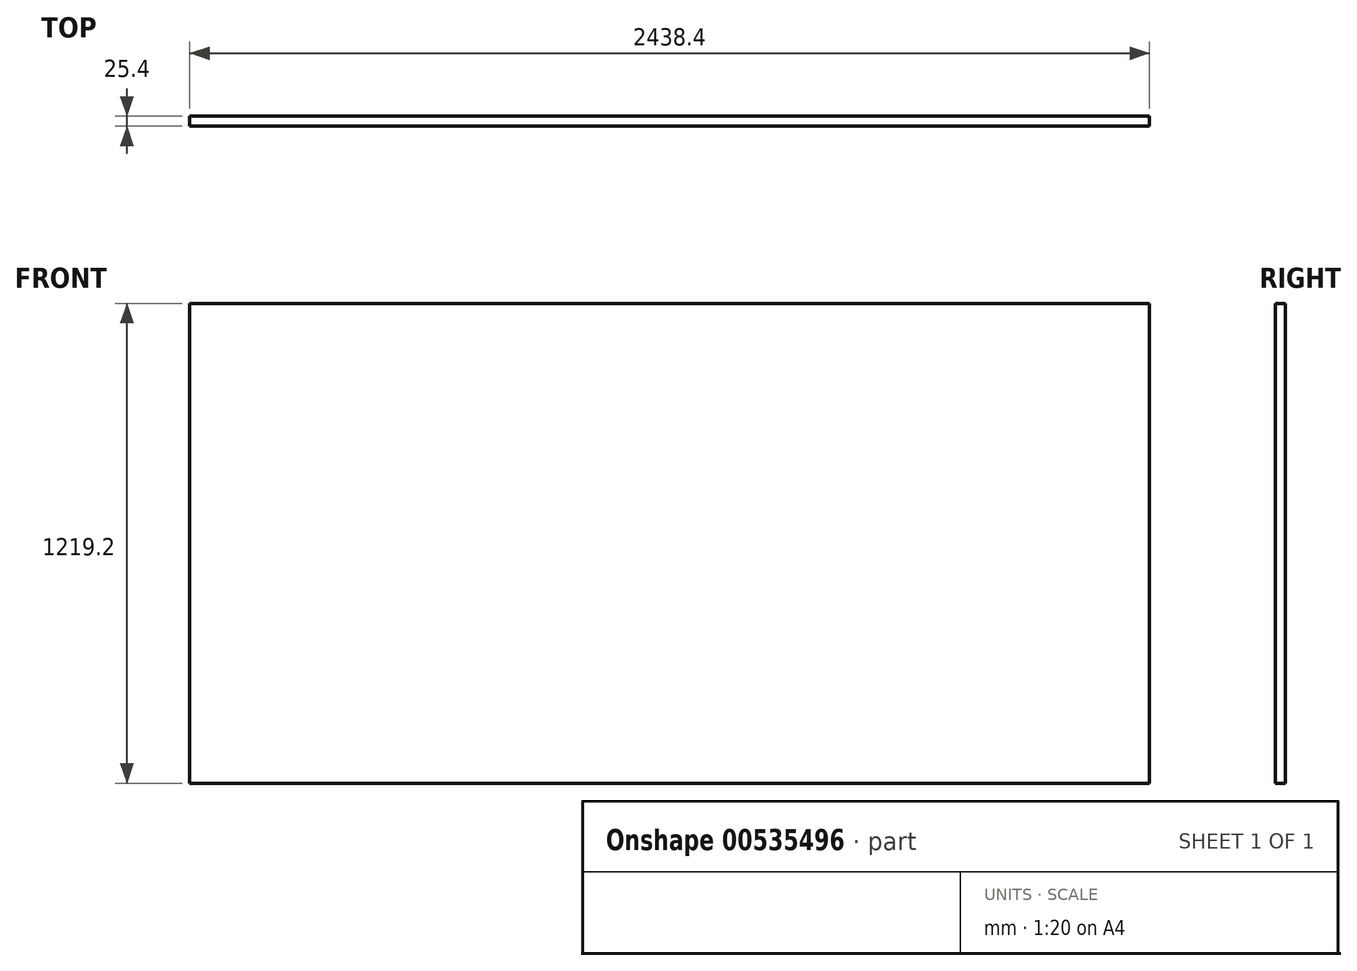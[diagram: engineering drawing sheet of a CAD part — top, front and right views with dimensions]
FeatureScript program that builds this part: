
annotation { "Feature Type Name" : "Feature", "Feature Type Description" : "" }
export const myFeature = defineFeature(function(context is Context, id is Id, definition is map)
    precondition{}
    {
        {
            var Q0;
            Q0=qCreatedBy(makeId("Front.planeOp"),FACE);
            var sketch = newSketch(context, id + "F0", { "sketchPlane" : qUnion([Q0])});
            skLineSegment(sketch, "E0.bottom", {"start": v(-1334.16, 605.52) * mm, "end": v(1104.24, 605.52) * mm});
            skLineSegment(sketch, "E0.top", {"start": v(-1334.16, -613.68) * mm, "end": v(1104.24, -613.68) * mm});
            skLineSegment(sketch, "E0.left", {"start": v(-1334.16, 605.52) * mm, "end": v(-1334.16, -613.68) * mm});
            skLineSegment(sketch, "E0.right", {"start": v(1104.24, 605.52) * mm, "end": v(1104.24, -613.68) * mm});
            skSolve(sketch);
        }
        {
            var Q0;
            Q0 = qSketchRegion(id + "F0", true);
            extrude(context, id + "F1", {"entities" : qUnion([Q0]), "depth" : 25.4 * mm, "offsetDistance" : 25.4 * mm});
        }
    });
